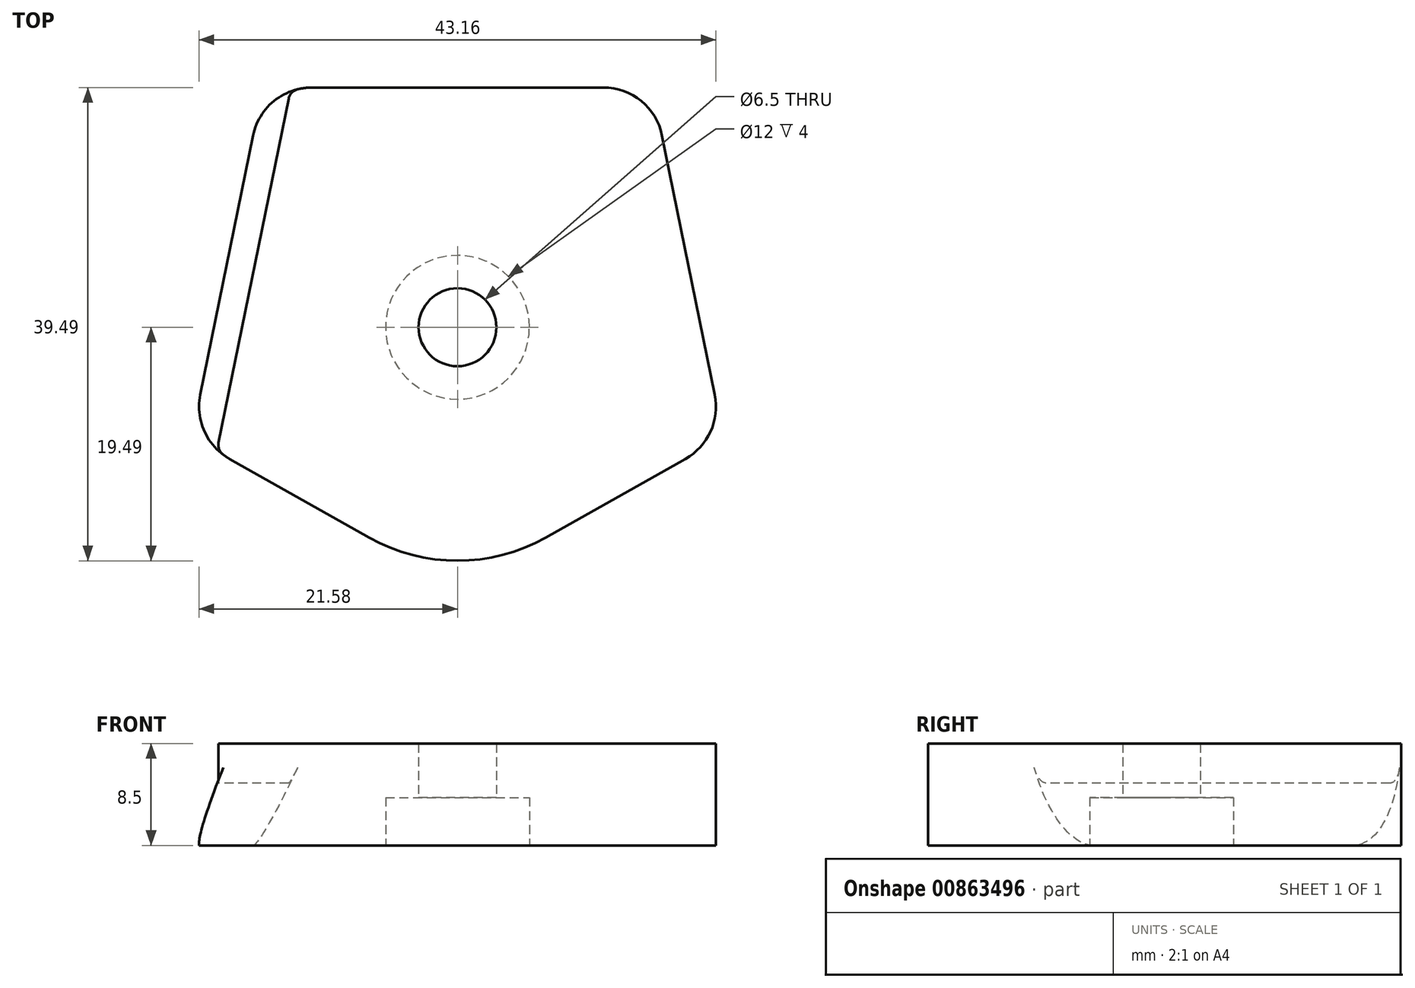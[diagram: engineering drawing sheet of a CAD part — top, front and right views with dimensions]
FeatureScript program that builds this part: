
annotation { "Feature Type Name" : "Feature", "Feature Type Description" : "" }
export const myFeature = defineFeature(function(context is Context, id is Id, definition is map)
    precondition{}
    {
        {
            var Q0;
            Q0=qCreatedBy(makeId("Top.planeOp"),FACE);
            var sketch = newSketch(context, id + "F0", { "sketchPlane" : qUnion([Q0])});
            skLineSegment(sketch, "E0", {"start": v(17.07, -4) * mm, "end": v(21.47, -25.63) * mm});
            skLineSegment(sketch, "E1", {"start": v(0, 0) * mm, "end": v(12.17, 0) * mm});
            skLineSegment(sketch, "E2", {"start": v(7.36, -37.56) * mm, "end": v(19.03, -30.99) * mm});
            skLineSegment(sketch, "E3", {"start": v(0, -15) * mm, "end": v(0, -20) * mm, "construction": true});
            skLineSegment(sketch, "E4.MirrorCS", {"start": v(0, 0) * mm, "end": v(-12.17, 0) * mm});
            skLineSegment(sketch, "E5.MirrorCS", {"start": v(-17.07, -4) * mm, "end": v(-21.47, -25.63) * mm});
            skLineSegment(sketch, "E6.MirrorCS", {"start": v(-7.36, -37.56) * mm, "end": v(-19.03, -30.99) * mm});
            skPoint(sketch, "E7.visualSharp", {"position": v(0, -41.7) * mm});
            skArc(sketch, "E7.filletArc", {"start": v(-7.36, -37.56) * mm, "mid": v(0, -39.49) * mm, "end": v(7.36, -37.56) * mm});
            skPoint(sketch, "E8.visualSharp", {"position": v(22.2, -29.2) * mm});
            skArc(sketch, "E8.filletArc", {"start": v(19.03, -30.99) * mm, "mid": v(21.12, -28.7) * mm, "end": v(21.47, -25.63) * mm});
            skPoint(sketch, "E9.visualSharp", {"position": v(-22.2, -29.2) * mm});
            skArc(sketch, "E9.filletArc", {"start": v(-21.47, -25.63) * mm, "mid": v(-21.12, -28.7) * mm, "end": v(-19.03, -30.99) * mm});
            skPoint(sketch, "E10.visualSharp", {"position": v(16.26, 0) * mm});
            skArc(sketch, "E10.filletArc", {"start": v(17.07, -4) * mm, "mid": v(15.34, -1.13) * mm, "end": v(12.17, 0) * mm});
            skPoint(sketch, "E11.visualSharp", {"position": v(-16.26, 0) * mm});
            skArc(sketch, "E11.filletArc", {"start": v(-12.17, 0) * mm, "mid": v(-15.34, -1.13) * mm, "end": v(-17.07, -4) * mm});
            skCircle(sketch, "E12", {"center": v(0, -20) * mm, "radius": 3.25 * mm});
            skSolve(sketch);
        }
        {
            var Q0;
            Q0 = qSketchRegion(id + "F0", true);
            extrude(context, id + "F1", {"entities" : qUnion([Q0]), "depth" : 8.5 * mm, "offsetDistance" : 25 * mm});
        }
        {
            var Q0;
            Q0=makeQuery(id+"F1.opExtrude","CAP_FACE",FACE,{"disambiguationData":[OSD([sQuery(id+"F0.wireOp",EDGE,"E0"),sQuery(id+"F0.wireOp",EDGE,"E1"),sQuery(id+"F0.wireOp",EDGE,"E2"),sQuery(id+"F0.wireOp",EDGE,"E4.MirrorCS"),sQuery(id+"F0.wireOp",EDGE,"E5.MirrorCS"),sQuery(id+"F0.wireOp",EDGE,"E6.MirrorCS"),sQuery(id+"F0.wireOp",EDGE,"E7.filletArc"),sQuery(id+"F0.wireOp",EDGE,"E8.filletArc"),sQuery(id+"F0.wireOp",EDGE,"E9.filletArc"),sQuery(id+"F0.wireOp",EDGE,"E10.filletArc"),sQuery(id+"F0.wireOp",EDGE,"E11.filletArc"),sQuery(id+"F0.wireOp",EDGE,"E12")])],"isStart":true});
            var sketch = newSketch(context, id + "F2", { "sketchPlane" : qUnion([Q0])});
            skCircle(sketch, "E13", {"center": v(0, 20) * mm, "radius": 6 * mm});
            skSolve(sketch);
        }
        {
            var Q0;
            Q0=makeQuery(id+"F2.imprint","IMPRINT",FACE,{"disambiguationData":[TD([[makeQuery(id+"F2.imprint","IMPRINT",EDGE,{"derivedFrom":sQuery(id+"F2.wireOp",EDGE,"E13")}),1.0]])]});
            extrude(context, id + "F3", {"entities" : qUnion([Q0]), "operationType" : NewBodyOperationType.REMOVE, "oppositeDirection" : true, "depth" : 4 * mm, "offsetDistance" : 25 * mm});
        }
        {
            var Q0;
            Q0=makeQuery(id+"F1.opExtrude","SWEPT_EDGE",EDGE,{"disambiguationData":[OSD([sQuery(id+"F0.wireOp",EDGE,"E5.MirrorCS"),sQuery(id+"F0.wireOp",EDGE,"E9.filletArc")])]});
            cPlane(context, id + "F4", {"entities" : qUnion([Q0]), "cplaneType" : CPlaneType.LINE_ANGLE, "offset" : 25 * mm, "angle" : 101.5 * degree, "width" : 150 * mm, "height" : 150 * mm});
        }
        {
            var Q0;
            Q0=qCreatedBy(id+"F4.planeOp",FACE);
            cPlane(context, id + "F5", {"entities" : qUnion([Q0]), "cplaneType" : CPlaneType.OFFSET, "offset" : 15 * mm, "oppositeDirection" : true, "width" : 150 * mm, "height" : 150 * mm});
        }
        {
            var Q0;
            Q0=qCreatedBy(id+"F5.planeOp",FACE);
            var sketch = newSketch(context, id + "F6", { "sketchPlane" : qUnion([Q0])});
            skLineSegment(sketch, "E14", {"start": v(15.93, 8.5) * mm, "end": v(15.93, 0) * mm});
            skLineSegment(sketch, "E15", {"start": v(13.63, 8.5) * mm, "end": v(13.63, 5.2) * mm});
            skLineSegment(sketch, "E16", {"start": v(13.63, 5.2) * mm, "end": v(15.93, 0) * mm});
            skLineSegment(sketch, "E17", {"start": v(13.63, 8.5) * mm, "end": v(15.93, 8.5) * mm});
            skSolve(sketch);
        }
        {
            var Q0;
            Q0 = qSketchRegion(id + "F6", true);
            extrude(context, id + "F7", {"entities" : qUnion([Q0]), "operationType" : NewBodyOperationType.REMOVE, "endBound" : BoundingType.THROUGH_ALL, "depth" : 25 * mm, "offsetDistance" : 25 * mm});
        }
        {
            var Q0;
            Q0=makeQuery(id+"F7.boolean.opBoolean","INTERSECT",EDGE,{"derivedFrom":[makeQuery(id+"F1.opExtrude","SWEPT_FACE",FACE,{"disambiguationData":[OSD([sQuery(id+"F0.wireOp",EDGE,"E9.filletArc")])]}),makeQuery(id+"F7.opExtrude","SWEPT_FACE",FACE,{"disambiguationData":[OSD([sQuery(id+"F6.wireOp",EDGE,"E15")])]})]});
            var Q1;
            Q1=makeQuery(id+"FVRlJIkksMSBwwc_1.1.F7.boolean.opBoolean","INTERSECT",EDGE,{"derivedFrom":[makeQuery(id+"F1.opExtrude","SWEPT_FACE",FACE,{"disambiguationData":[OSD([sQuery(id+"F0.wireOp",EDGE,"E8.filletArc")])]}),makeQuery(id+"FVRlJIkksMSBwwc_1.1.F7.opExtrude","SWEPT_FACE",FACE,{"disambiguationData":[OSD([sQuery(id+"FVRlJIkksMSBwwc_1.1.F6.wireOp",EDGE,"E15")])]})]});
            var Q2;
            Q2=makeQuery(id+"F7.boolean.opBoolean","INTERSECT",EDGE,{"derivedFrom":[makeQuery(id+"F1.opExtrude","SWEPT_FACE",FACE,{"disambiguationData":[OSD([sQuery(id+"F0.wireOp",EDGE,"E11.filletArc")])]}),makeQuery(id+"F7.opExtrude","SWEPT_FACE",FACE,{"disambiguationData":[OSD([sQuery(id+"F6.wireOp",EDGE,"E15")])]})]});
            var Q3;
            Q3=makeQuery(id+"FVRlJIkksMSBwwc_1.1.F7.boolean.opBoolean","INTERSECT",EDGE,{"derivedFrom":[makeQuery(id+"F1.opExtrude","SWEPT_FACE",FACE,{"disambiguationData":[OSD([sQuery(id+"F0.wireOp",EDGE,"E10.filletArc")])]}),makeQuery(id+"FVRlJIkksMSBwwc_1.1.F7.opExtrude","SWEPT_FACE",FACE,{"disambiguationData":[OSD([sQuery(id+"FVRlJIkksMSBwwc_1.1.F6.wireOp",EDGE,"E15")])]})]});
            fillet(context, id + "F8", {"entities" : qUnion([Q0, Q1, Q2, Q3]), "radius" : 1 * mm, "tangentPropagation" : true, "allowEdgeOverflow" : false});
        }
    });
